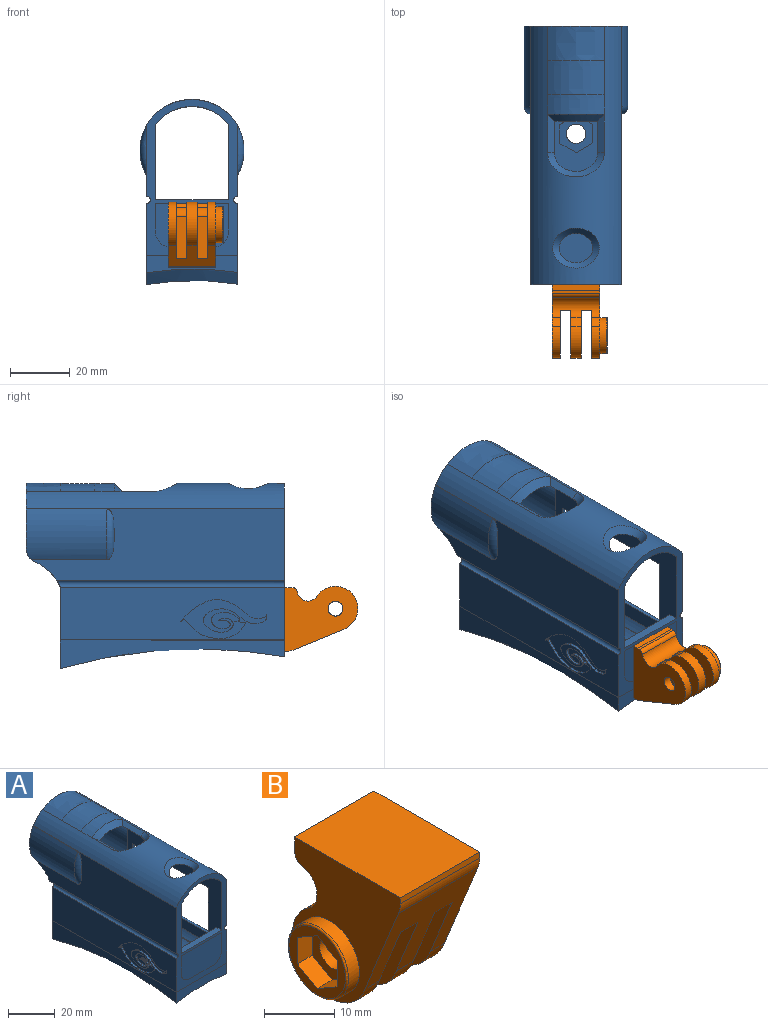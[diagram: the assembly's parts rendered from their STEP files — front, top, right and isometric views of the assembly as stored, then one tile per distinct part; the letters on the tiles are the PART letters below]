
ASSEMBLY  parts=2 mates=1
PART A: 79 faces, bbox 47.7x101.8x77.8 mm
  f0: cylinder r=4mm len=72mm, axis (0,-1,0), area 18.4mm2, adj f2,f48,f77,f78
  f1: cylinder r=4mm len=72mm, axis (0,1,0), area 12.7mm2, adj f2,f48,f75,f76
  f2: plane 24.4x14.54mm, normal (0,1,0), area 334mm2, adj f0,f1,f3,f4,f5,f73,f75,f76
  f3: plane 86.5x36mm, normal (1,0,0), area 2416.2mm2, adj f2,f11,f13,f17,f19,f26,f34,f48
  f4: plane 86.5x36mm, normal (-1,0,0), area 1311.5mm2, adj f2,f12,f13,f17,f18,f26,f33,f36
  f5: plane 72x14.4mm, normal (0,0,1), area 830.5mm2, adj f2,f48,f60,f61,f62,f63,f64,f65
  f6: plane 12.59x11.02mm, normal (0,0,1), area 64.7mm2, adj f56,f66,f67,f68,f69,f70,f71
  f7: plane 12.59x11.02mm, normal (0,0,1), area 70mm2, adj f55,f60,f61,f62,f63,f64,f65
  f8: plane 30.41x5.64mm, normal (0,-1,0), area 144.2mm2, adj f26,f42,f43,f57,f58,f59
  f9: plane 30.41x9.59mm, normal (0,1,0), area 263.6mm2, adj f42,f48,f57,f58,f59
  f10: plane 75.01x17.54mm, normal (-1,0,0), area 1118.6mm2, adj f24,f26,f43,f48,f53
  f11: cylinder r=16.78mm len=3mm, axis (1,0,0), area 2.3mm2, adj f3,f24,f48,f50
  f12: cylinder r=16.78mm len=3mm, axis (1,0,0), area 2.3mm2, adj f4,f47,f48,f49
  f13: plane 34.85x21.69mm, normal (0,1,0), area 153.1mm2, adj f3,f4,f14,f15,f16,f17,f18,f19
  f14: extruded ~14.56x11.5mm, area 173.9mm2, adj f13,f17,f38
  f15: plane 96.52x33.98mm, normal (1,0,0), area 499.9mm2, adj f13,f20,f23,f26,f37,f39,f44,f45
  f16: plane 96.51x33.98mm, normal (-1,0,0), area 1539.1mm2, adj f13,f21,f23,f24,f26,f40,f50,f51
  f17: cylinder r=15.29mm len=86.5mm, axis (0,-1,0), area 1639.3mm2, adj f3,f4,f13,f14,f26,f29,f30,f32
  f18: cylinder r=14.7mm len=29.5mm, axis (0,1,0), area 510mm2, adj f4,f13,f33,f52
  f19: cylinder r=14.7mm len=29.5mm, axis (0,1,0), area 508.1mm2, adj f3,f13,f34,f51
  f20: cylinder r=17.44mm len=27mm, axis (0,1,0), area 478.7mm2, adj f13,f15,f39,f52
  f21: cylinder r=17.44mm len=27mm, axis (0,1,0), area 477.8mm2, adj f13,f16,f40,f51
  f22: extruded ~19.03x11.5mm, area 230.6mm2, adj f13,f23,f31
  f23: cylinder r=17.95mm len=86.5mm, axis (0,1,0), area 1992.6mm2, adj f13,f15,f16,f22,f26,f28,f29,f30
  f24: cylinder r=1.25mm len=76.35mm, axis (0,1,0), area 297.6mm2, adj f10,f11,f16,f26,f48,f50
  f25: plane 75x17.53mm, normal (1,0,0), area 923.3mm2, adj f26,f36,f42,f44,f45,f46,f47,f48
  f26: plane 52.4x30.4mm, normal (0,-1,0), area 449.8mm2, adj f3,f4,f8,f10,f15,f16,f17,f23
  f27: bspline ~20.52x5.47mm, area 58.2mm2, adj f28,f32,f35,f41
  f28: extruded ~19.03x6.5mm, area 130.2mm2, adj f23,f27,f31
  f29: bspline ~15.53x13.39mm, area 101.3mm2, adj f17,f23
  f30: bspline ~19.04x8.2mm, area 61.9mm2, adj f17,f23,f32,f35
  f31: extruded ~19.03x11.53mm, area 231.1mm2, adj f22,f23,f28
  f32: plane 12.81x2.24mm, normal (-0.54,0,0.84), area 30.9mm2, adj f17,f23,f27,f30
  f33: plane 16.36x2.49mm, normal (0,1,0), area 27.6mm2, adj f4,f18
  f34: plane 16.34x2.48mm, normal (0,1,0), area 27.5mm2, adj f3,f19
  f35: plane 12.82x2.24mm, normal (0.54,0,0.84), area 31mm2, adj f17,f23,f27,f30
  f36: cylinder r=3mm len=52mm, axis (0,1,0), area 230.9mm2, adj f4,f25,f44,f45
  f37: cylinder r=3mm len=52mm, axis (0,-1,0), area 230.9mm2, adj f4,f15,f44,f45
  f38: extruded ~14.56x11.53mm, area 174.3mm2, adj f14,f17,f41
  f39: torus R=14.94mm, axis (0,-1,0), area 0mm2, adj f15,f20
  f40: torus R=14.94mm, axis (0,-1,0), area 0mm2, adj f16,f21
  f41: extruded ~14.56x8.84mm, area 133.6mm2, adj f17,f27,f38
  f42: bspline ~81.3x15.34mm, area 75.1mm2, adj f8,f9,f25,f58
  f43: cylinder r=113.79mm len=75mm, axis (0,1,0), area 1.6mm2, adj f8,f10,f59
  f44: cylinder r=3mm len=30mm, axis (0,0,-1), area 121.1mm2, adj f4,f15,f25,f36,f37,f46
  f45: cylinder r=3mm len=30mm, axis (0,0,1), area 121.1mm2, adj f4,f15,f25,f36,f37,f47
  f46: cylinder r=1.25mm len=7.44mm, axis (0,1,0), area 27.2mm2, adj f15,f25,f26,f44
  f47: cylinder r=1.25mm len=21.79mm, axis (0,1,0), area 80.6mm2, adj f12,f15,f25,f45,f49
  f48: plane 30.4x17.54mm, normal (0,1,0), area 199mm2, adj f0,f1,f3,f4,f5,f9,f10,f11
  f49: cylinder r=16.78mm len=8.13mm, axis (-1,0,0), area 33.2mm2, adj f4,f12,f15,f47,f52
  f50: cylinder r=16.78mm len=8.13mm, axis (-1,0,0), area 33.2mm2, adj f3,f11,f16,f24,f51
  f51: cylinder r=5mm len=4.6mm, axis (-1,0,0), area 17.4mm2, adj f3,f13,f16,f19,f21,f50
  f52: cylinder r=5mm len=4.6mm, axis (-1,0,0), area 17.4mm2, adj f4,f13,f15,f18,f20,f49
  f53: extruded ~28.69x12.85mm, area 93mm2, adj f10,f54
  f54: plane 29.12x13.26mm, normal (-1,0,0), area 152.7mm2, adj f53
  f55: cylinder r=3.25mm len=6.5mm, axis (0,0,1), area 45.8mm2, adj f7,f57
  f56: cylinder r=3.5mm len=7mm, axis (0,0,1), area 20.3mm2, adj f6,f57
  f57: revolved ~75.59x30.41mm, area 2241.2mm2, adj f8,f9,f55,f56,f58,f59
  f58: plane 75.01x8.44mm, normal (1,0,0), area 267.8mm2, adj f8,f9,f42,f57
  f59: plane 75.01x9.59mm, normal (-1,0,0), area 352.3mm2, adj f8,f9,f43,f57
  f60: plane 5.44x4mm, normal (0.51,-0.86,0), area 25.4mm2, adj f5,f7,f61,f62
  f61: plane 5.49x4mm, normal (-0.49,-0.87,0), area 25.1mm2, adj f5,f7,f60,f64
  f62: plane 6.28x4mm, normal (1,0.01,0), area 25.1mm2, adj f5,f7,f60,f63
  f63: plane 5.49x4mm, normal (0.49,0.87,0), area 25.1mm2, adj f5,f7,f62,f65
  f64: plane 6.28x4mm, normal (-1,-0.01,0), area 25.1mm2, adj f5,f7,f61,f65
  f65: plane 5.44x4mm, normal (-0.51,0.86,0), area 25.4mm2, adj f5,f7,f63,f64
  f66: plane 5.44x4mm, normal (-0.51,0.86,0), area 25.4mm2, adj f5,f6,f67,f69
  f67: plane 6.28x4mm, normal (-1,-0.01,0), area 25.1mm2, adj f5,f6,f66,f68
  f68: plane 5.49x4mm, normal (-0.49,-0.87,0), area 25.1mm2, adj f5,f6,f67,f70
  f69: plane 5.49x4mm, normal (0.49,0.87,0), area 25.1mm2, adj f5,f6,f66,f71
  f70: plane 5.44x4mm, normal (0.51,-0.86,0), area 25.4mm2, adj f5,f6,f68,f71
  f71: plane 6.28x4mm, normal (1,0.01,0), area 25.1mm2, adj f5,f6,f69,f70
  f72: plane 24.4x14.53mm, normal (0,-1,0), area 343.9mm2, adj f26
  f73: plane 24.4x1.25mm, normal (0,1,0), area 30.5mm2, adj f2,f3,f4,f74
  f74: plane 24.4x3mm, normal (0,0,1), area 73.2mm2, adj f3,f4,f26,f73
  f75: cylinder r=13.71mm len=72mm, axis (0,1,0), area 251.1mm2, adj f1,f2,f5,f48
  f76: cylinder r=13.71mm len=72mm, axis (0,1,0), area 251.1mm2, adj f1,f2,f4,f48
  f77: cylinder r=13.73mm len=72mm, axis (0,1,0), area 248.3mm2, adj f0,f2,f3,f48
  f78: cylinder r=13.73mm len=72mm, axis (0,1,0), area 248.3mm2, adj f0,f2,f5,f48
PART B: 35 faces, bbox 18.5x21.8x24.6 mm
  f0: plane 16.59x16mm, normal (0,-0.93,-0.38), area 205.7mm2, adj f1,f2,f3,f4,f5,f8,f10,f13
  f1: plane 18.98x15.81mm, normal (1,0,0), area 197.6mm2, adj f0,f13,f14,f24,f32,f34
  f2: plane 18.98x15.81mm, normal (-1,0,0), area 197.6mm2, adj f0,f13,f14,f24,f32,f33
  f3: plane 24.59x21.75mm, normal (1,0,0), area 357.2mm2, adj f0,f6,f7,f8,f24,f25,f26,f27
  f4: plane 24.59x21.75mm, normal (-1,0,0), area 263.7mm2, adj f0,f6,f10,f11,f24,f25,f26,f27
  f5: plane 18.98x15.81mm, normal (1,0,0), area 197.6mm2, adj f0,f9,f10,f24,f31,f33
  f6: plane 16x0.9mm, normal (0,1,-0.07), area 14.4mm2, adj f3,f4,f25,f26
  f7: cylinder r=2.5mm len=5mm, axis (-1,0,0), area 44mm2, adj f3,f23
  f8: cylinder r=7.5mm len=14.6mm, axis (-1,0,0), area 67.6mm2, adj f0,f3,f23,f30
  f9: cylinder r=2.5mm len=5mm, axis (-1,0,0), area 36.1mm2, adj f5,f15
  f10: cylinder r=7.5mm len=14.6mm, axis (-1,0,0), area 67.6mm2, adj f0,f4,f5,f31
  f11: cylinder r=6mm len=12mm, axis (1,0,0), area 82.9mm2, adj f4,f22
  f12: plane 11.4x11.4mm, normal (-1,0,0), area 46.6mm2, adj f16,f17,f18,f19,f20,f21,f22
  f13: cylinder r=7.5mm len=14.6mm, axis (-1,0,0), area 82mm2, adj f0,f1,f2,f32
  f14: cylinder r=2.5mm len=5mm, axis (-1,0,0), area 53.4mm2, adj f1,f2
  f15: plane 9.24x8mm, normal (-1,0,0), area 35.8mm2, adj f9,f16,f17,f18,f19,f20,f21
  f16: plane 4x3mm, normal (0,0.5,-0.87), area 13.9mm2, adj f12,f15,f17,f21
  f17: plane 4x3mm, normal (0,-0.5,-0.87), area 13.9mm2, adj f12,f15,f16,f18
  f18: plane 4.62x3mm, normal (0,-1,0), area 13.9mm2, adj f12,f15,f17,f19
  f19: plane 4x3mm, normal (0,-0.5,0.87), area 13.9mm2, adj f12,f15,f18,f20
  f20: plane 4x3mm, normal (0,0.5,0.87), area 13.9mm2, adj f12,f15,f19,f21
  f21: plane 4.62x3mm, normal (0,1,0), area 13.9mm2, adj f12,f15,f16,f20
  f22: torus R=5.7mm, axis (-1,0,0), area 17.4mm2, adj f11,f12
  f23: plane 18.98x15.81mm, normal (-1,0,0), area 197.6mm2, adj f0,f7,f8,f24,f30,f34
  f24: cylinder r=3.68mm len=16mm, axis (1,0,0), area 125.2mm2, adj f1,f2,f3,f4,f5,f23,f25,f30
  f25: cylinder r=1.5mm len=16mm, axis (1,0,0), area 32.6mm2, adj f3,f4,f6,f24
  f26: plane 16x2mm, normal (0,1,0), area 32mm2, adj f3,f4,f6,f28
  f27: plane 16x1.02mm, normal (0,-1,0), area 16.3mm2, adj f3,f4,f28,f29
  f28: plane 21.31x16mm, normal (0,0,1), area 341mm2, adj f3,f4,f26,f27
  f29: cylinder r=5mm len=16mm, axis (-1,0,0), area 31mm2, adj f0,f3,f4,f27
  f30: cylinder r=7.09mm len=3.03mm, axis (-1,0,0), area 11.1mm2, adj f3,f8,f23,f24
  f31: cylinder r=7.09mm len=3.03mm, axis (-1,0,0), area 11.1mm2, adj f4,f5,f10,f24
  f32: cylinder r=7.09mm len=3.4mm, axis (-1,0,0), area 13.5mm2, adj f1,f2,f13,f24
  f33: plane 14.14x3.5mm, normal (0,0,-1), area 49.5mm2, adj f0,f2,f5,f24
  f34: plane 14.14x3.5mm, normal (0,0,-1), area 49.5mm2, adj f0,f1,f23,f24
PLACE A t=(-55.04,11.17,-13.9)mm
PLACE B rot(axis=(0,0.71,0.71),180deg) t=(-4.76,-59.85,-3.43)mm
MATE planar B.f28 <-> A.f72  axis (0,1,0) through (-4.76,-42.76,-7.02)mm
